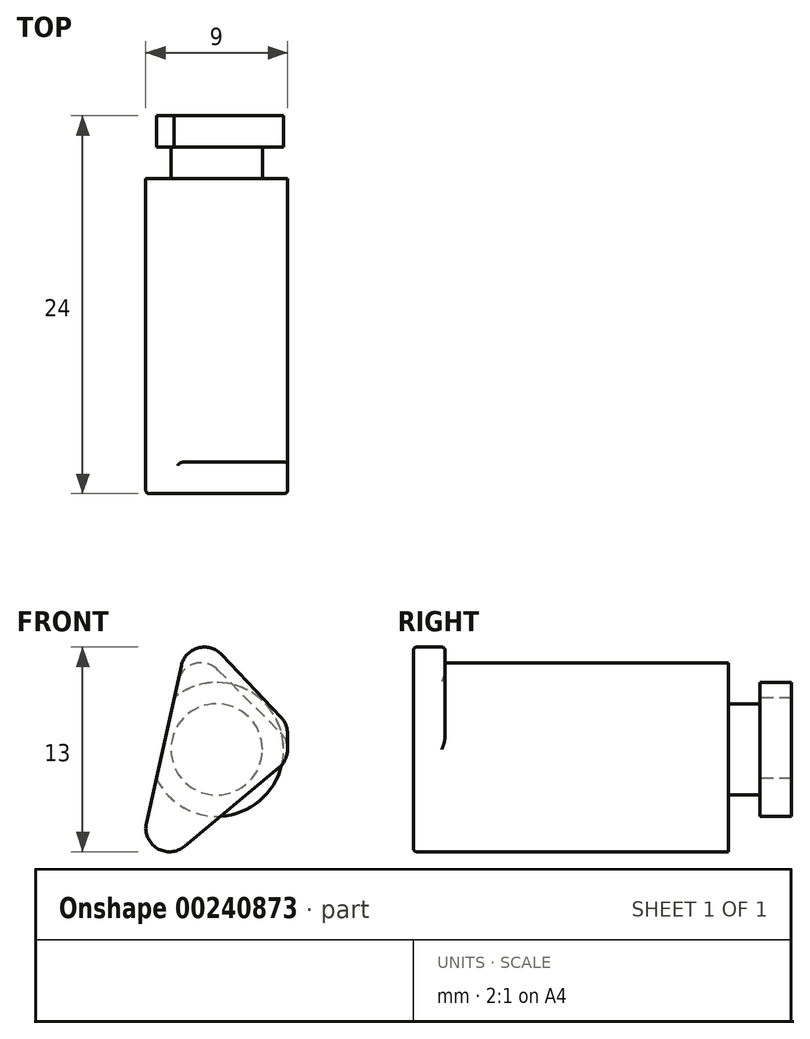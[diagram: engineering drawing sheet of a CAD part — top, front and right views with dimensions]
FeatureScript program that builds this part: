
annotation { "Feature Type Name" : "Feature", "Feature Type Description" : "" }
export const myFeature = defineFeature(function(context is Context, id is Id, definition is map)
    precondition{}
    {
        {
            var Q0;
            Q0=qCreatedBy(makeId("Front.planeOp"),FACE);
            var sketch = newSketch(context, id + "F0", { "sketchPlane" : qUnion([Q0])});
            skCircle(sketch, "E0", {"center": v(0, 0) * mm, "radius": 2.9 * mm});
            skLineSegment(sketch, "E1", {"start": v(0.41, 5.41) * mm, "end": v(4.41, 1.41) * mm, "construction": true});
            skLineSegment(sketch, "E2", {"start": v(4.28, -1.54) * mm, "end": v(-1.72, -6.54) * mm, "construction": true});
            skLineSegment(sketch, "E3", {"start": v(-4.95, -4.57) * mm, "end": v(-2.95, 4.43) * mm, "construction": true});
            skPoint(sketch, "E4.visualSharp", {"position": v(-2.16, 8) * mm});
            skArc(sketch, "E4.filletArc", {"start": v(0.41, 5.41) * mm, "mid": v(-1.56, 5.92) * mm, "end": v(-2.95, 4.43) * mm, "construction": true});
            skPoint(sketch, "E5.visualSharp", {"position": v(5.96, -0.13) * mm});
            skArc(sketch, "E5.filletArc", {"start": v(4.28, -1.54) * mm, "mid": v(5, -0.1) * mm, "end": v(4.41, 1.41) * mm, "construction": true});
            skPoint(sketch, "E6.visualSharp", {"position": v(-6.22, -10.3) * mm});
            skArc(sketch, "E6.filletArc", {"start": v(-4.95, -4.57) * mm, "mid": v(-4.04, -6.7) * mm, "end": v(-1.72, -6.54) * mm, "construction": true});
            skArc(sketch, "E7.0", {"start": v(0.06, 5.06) * mm, "mid": v(-1.42, 5.44) * mm, "end": v(-2.46, 4.33) * mm});
            skArc(sketch, "E7.1", {"start": v(3.96, -1.15) * mm, "mid": v(4.5, -0.07) * mm, "end": v(4.06, 1.06) * mm});
            skLineSegment(sketch, "E7.2", {"start": v(3.96, -1.15) * mm, "end": v(-2.04, -6.15) * mm});
            skLineSegment(sketch, "E7.3", {"start": v(0.06, 5.06) * mm, "end": v(4.06, 1.06) * mm});
            skArc(sketch, "E7.4", {"start": v(-4.46, -4.67) * mm, "mid": v(-3.78, -6.28) * mm, "end": v(-2.04, -6.15) * mm});
            skLineSegment(sketch, "E7.5", {"start": v(-4.46, -4.67) * mm, "end": v(-2.46, 4.33) * mm});
            skSolve(sketch);
        }
        {
            var Q0;
            Q0=makeQuery(id+"F0.imprint","IMPRINT",FACE,{"disambiguationData":[TD([[makeQuery(id+"F0.imprint","IMPRINT",EDGE,{"derivedFrom":sQuery(id+"F0.wireOp",EDGE,"E0")}),1.0]])]});
            extrude(context, id + "F1", {"entities" : qUnion([Q0]), "oppositeDirection" : true, "depth" : 2 * mm});
        }
        {
            var Q0;
            Q0=makeQuery(id+"F0.imprint","IMPRINT",FACE,{"disambiguationData":[TD([[makeQuery(id+"F0.imprint","IMPRINT",EDGE,{"derivedFrom":sQuery(id+"F0.wireOp",EDGE,"E0")}),-1.0]])]});
            var Q1;
            Q1=makeQuery(id+"F0.imprint","IMPRINT",FACE,{"disambiguationData":[TD([[makeQuery(id+"F0.imprint","IMPRINT",EDGE,{"derivedFrom":sQuery(id+"F0.wireOp",EDGE,"E0")}),1.0]])]});
            extrude(context, id + "F2", {"entities" : qUnion([Q0, Q1]), "operationType" : NewBodyOperationType.ADD, "depth" : 18 * mm});
        }
        {
            var Q0;
            Q0=makeQuery(id+"F2.opExtrude","CAP_FACE",FACE,{"disambiguationData":[OSD([sQuery(id+"F0.wireOp",EDGE,"E7.0"),sQuery(id+"F0.wireOp",EDGE,"E7.1"),sQuery(id+"F0.wireOp",EDGE,"E7.2"),sQuery(id+"F0.wireOp",EDGE,"E7.3"),sQuery(id+"F0.wireOp",EDGE,"E7.4"),sQuery(id+"F0.wireOp",EDGE,"E7.5")])],"isStart":false});
            var sketch = newSketch(context, id + "F3", { "sketchPlane" : qUnion([Q0])});
            skPoint(sketch, "E8", {"position": v(-1, 4) * mm});
            skPoint(sketch, "E9", {"position": v(3, 0) * mm});
            skPoint(sketch, "E10", {"position": v(-3, -5) * mm});
            skArc(sketch, "E11", {"start": v(0.31, 6.03) * mm, "mid": v(-1.18, 6.45) * mm, "end": v(-2.24, 5.33) * mm});
            skArc(sketch, "E12", {"start": v(4.5, 1) * mm, "mid": v(4.4, 1.55) * mm, "end": v(4.1, 2.03) * mm});
            skLineSegment(sketch, "E13", {"start": v(0.31, 6.03) * mm, "end": v(4.1, 2.03) * mm});
            skLineSegment(sketch, "E14", {"start": v(-2.24, 5.33) * mm, "end": v(-4.46, -4.67) * mm});
            skArc(sketch, "E15", {"start": v(-4.46, -4.67) * mm, "mid": v(-3.78, -6.28) * mm, "end": v(-2.04, -6.15) * mm});
            skLineSegment(sketch, "E16", {"start": v(4.5, 1) * mm, "end": v(4.5, 0) * mm});
            skArc(sketch, "E17.0", {"start": v(3.96, -1.15) * mm, "mid": v(4.36, -0.64) * mm, "end": v(4.5, 0) * mm});
            skPoint(sketch, "E18.orphan", {"position": v(4.06, 1.06) * mm});
            skLineSegment(sketch, "E19", {"start": v(3.96, -1.15) * mm, "end": v(-2.04, -6.15) * mm});
            skSolve(sketch);
        }
        {
            var Q0;
            Q0 = qSketchRegion(id + "F3", true);
            extrude(context, id + "F4", {"entities" : qUnion([Q0]), "operationType" : NewBodyOperationType.ADD, "depth" : 2 * mm});
        }
        {
            var Q0;
            Q0=makeQuery(id+"F4.opExtrude","CAP_FACE",FACE,{"disambiguationData":[OSD([sQuery(id+"F3.wireOp",EDGE,"E11"),sQuery(id+"F3.wireOp",EDGE,"E12"),sQuery(id+"F3.wireOp",EDGE,"E13"),sQuery(id+"F3.wireOp",EDGE,"E14"),sQuery(id+"F3.wireOp",EDGE,"E15"),sQuery(id+"F3.wireOp",EDGE,"E16"),sQuery(id+"F3.wireOp",EDGE,"E17.0"),sQuery(id+"F3.wireOp",EDGE,"E19")])],"isStart":false});
            var Q1;
            Q1=makeQuery(id+"F2.opExtrude","CAP_EDGE",EDGE,{"disambiguationData":[OSD([sQuery(id+"F0.wireOp",EDGE,"E7.0")])],"isStart":false});
            var Q2;
            Q2=makeQuery(id+"F4.opExtrude","CAP_EDGE",EDGE,{"disambiguationData":[OSD([sQuery(id+"F3.wireOp",EDGE,"E11")])],"isStart":true});
            fillet(context, id + "F5", {"entities" : qUnion([Q0, Q1, Q2]), "radius" : 0.2 * mm, "tangentPropagation" : true, "allowEdgeOverflow" : false});
        }
        {
            var Q0;
            Q0=makeQuery(id+"F1.opExtrude","CAP_FACE",FACE,{"disambiguationData":[OSD([sQuery(id+"F0.wireOp",EDGE,"E0")])],"isStart":false});
            var sketch = newSketch(context, id + "F6", { "sketchPlane" : qUnion([Q0])});
            skCircle(sketch, "E20", {"center": v(0, 0) * mm, "radius": 4.25 * mm});
            skSolve(sketch);
        }
        {
            var Q0;
            Q0=makeQuery(id+"F6.imprint","IMPRINT",FACE,{"disambiguationData":[TD([[makeQuery(id+"F6.imprint","IMPRINT",EDGE,{"derivedFrom":makeQuery(id+"F1.opExtrude","CAP_EDGE",EDGE,{"disambiguationData":[OSD([sQuery(id+"F0.wireOp",EDGE,"E0")])],"isStart":false})}),-1.0]])]});
            var Q1;
            Q1=makeQuery(id+"F6.imprint","IMPRINT",FACE,{"disambiguationData":[TD([[makeQuery(id+"F6.imprint","IMPRINT",EDGE,{"derivedFrom":sQuery(id+"F6.wireOp",EDGE,"E20")}),1.0]])]});
            extrude(context, id + "F7", {"entities" : qUnion([Q0, Q1]), "operationType" : NewBodyOperationType.ADD, "depth" : 2 * mm});
        }
        {
            var Q0;
            Q0=qCreatedBy(makeId("Front.planeOp"),FACE);
            var sketch = newSketch(context, id + "F8", { "sketchPlane" : qUnion([Q0])});
            skLineSegment(sketch, "E21.0", {"start": v(-4.46, -4.67) * mm, "end": v(-2.46, 4.33) * mm, "construction": true});
            skLineSegment(sketch, "E22", {"start": v(-2.46, 4.33) * mm, "end": v(-4.46, -4.67) * mm});
            skLineSegment(sketch, "E23", {"start": v(-6.2, 1.27) * mm, "end": v(-2.46, 4.33) * mm});
            skLineSegment(sketch, "E24", {"start": v(-6.2, 1.27) * mm, "end": v(-4.46, -4.67) * mm});
            skSolve(sketch);
        }
        {
            var Q0;
            Q0=makeQuery(id+"F8.imprint","IMPRINT",FACE,{"disambiguationData":[TD([[makeQuery(id+"F8.imprint","IMPRINT",EDGE,{"derivedFrom":sQuery(id+"F8.wireOp",EDGE,"E22")}),-1.0]])]});
            var Q1;
            Q1=sQuery(id+"F8.wireOp",EDGE,"E22");
            var Q2;
            Q2=sQuery(id+"F8.wireOp",EDGE,"E23");
            var Q3;
            Q3=sQuery(id+"F8.wireOp",EDGE,"E24");
            extrude(context, id + "F9", {"entities" : qUnion([Q0]), "operationType" : NewBodyOperationType.REMOVE, "surfaceEntities" : qUnion([Q1, Q2, Q3]), "endBound" : BoundingType.THROUGH_ALL, "oppositeDirection" : true, "depth" : 25 * mm});
        }
    });
